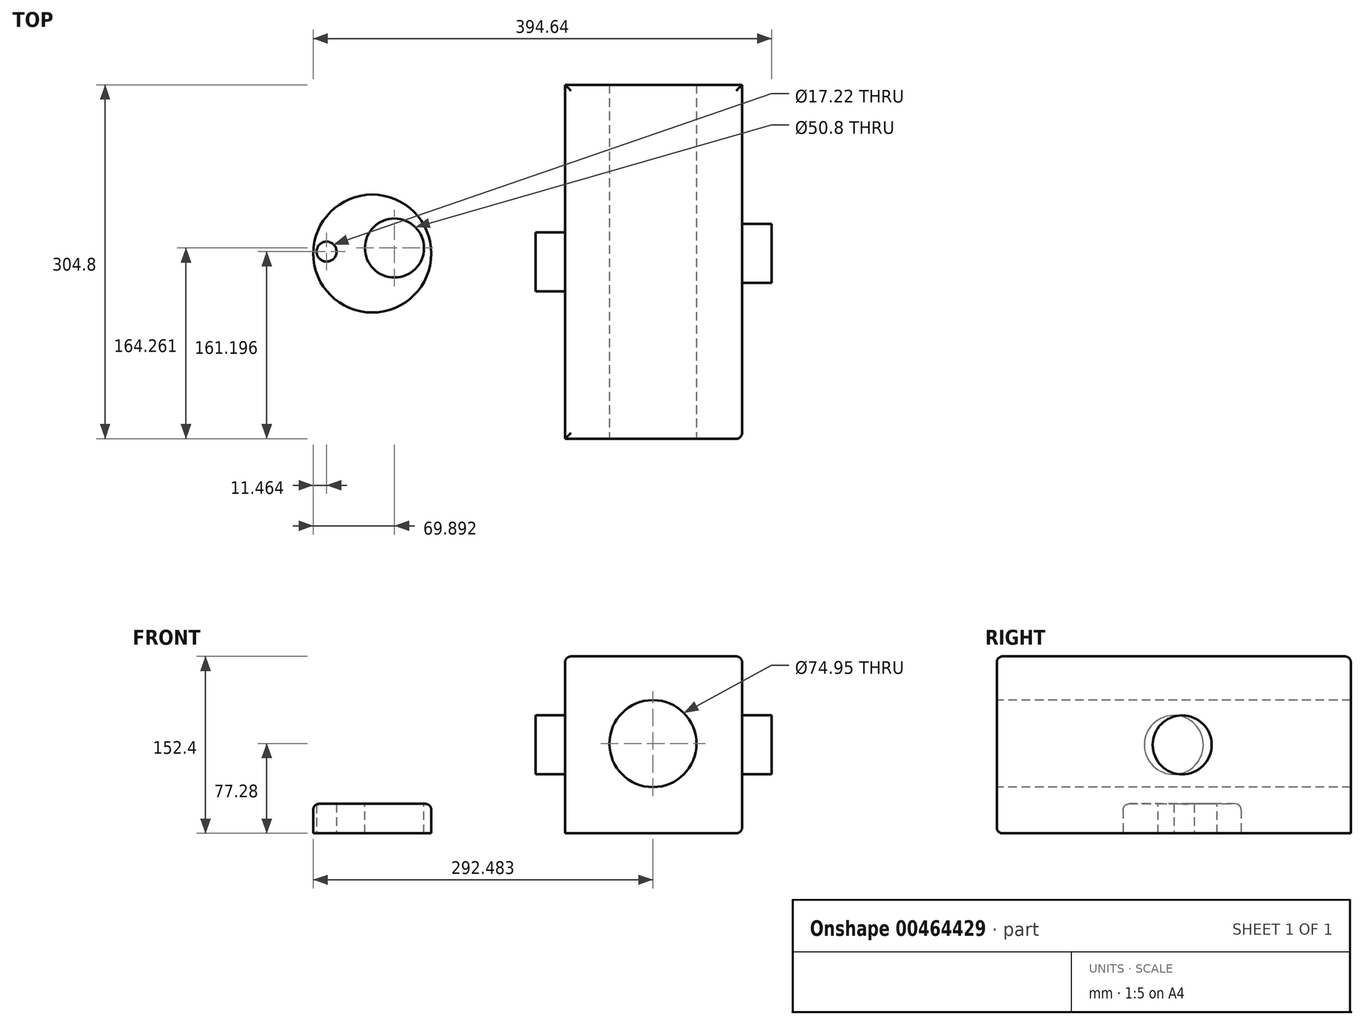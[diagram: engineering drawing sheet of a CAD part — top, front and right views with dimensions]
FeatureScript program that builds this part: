
annotation { "Feature Type Name" : "Feature", "Feature Type Description" : "" }
export const myFeature = defineFeature(function(context is Context, id is Id, definition is map)
    precondition{}
    {
        {
            var Q0;
            Q0=qCreatedBy(makeId("Top.planeOp"),FACE);
            var sketch = newSketch(context, id + "F0", { "sketchPlane" : qUnion([Q0])});
            skCircle(sketch, "E0", {"center": v(0, 0) * mm, "radius": 50.8 * mm});
            skLineSegment(sketch, "E1", {"start": v(0, 0) * mm, "end": v(-50.76, 2.14) * mm, "construction": true});
            skCircle(sketch, "E2", {"center": v(-39.34, 1.66) * mm, "radius": 8.61 * mm});
            skSolve(sketch);
        }
        {
            var Q0;
            Q0=makeQuery(id+"F0.imprint","IMPRINT",FACE,{"disambiguationData":[TD([[makeQuery(id+"F0.imprint","IMPRINT",EDGE,{"derivedFrom":sQuery(id+"F0.wireOp",EDGE,"E0")}),1.0]])]});
            extrude(context, id + "F1", {"entities" : qUnion([Q0]), "depth" : 25.4 * mm});
        }
        {
            var Q0;
            Q0=qCreatedBy(makeId("Top.planeOp"),FACE);
            var sketch = newSketch(context, id + "F2", { "sketchPlane" : qUnion([Q0])});
            skLineSegment(sketch, "E3.bottom", {"start": v(166.04, 145.26) * mm, "end": v(318.44, 145.26) * mm});
            skLineSegment(sketch, "E3.top", {"start": v(166.04, -159.54) * mm, "end": v(318.44, -159.54) * mm});
            skLineSegment(sketch, "E3.left", {"start": v(166.04, 145.26) * mm, "end": v(166.04, -159.54) * mm});
            skLineSegment(sketch, "E3.right", {"start": v(318.44, 145.26) * mm, "end": v(318.44, -159.54) * mm});
            skSolve(sketch);
        }
        {
            var Q0;
            Q0=makeQuery(id+"F2.imprint","IMPRINT",FACE,{"disambiguationData":[TD([[makeQuery(id+"F2.imprint","IMPRINT",EDGE,{"derivedFrom":sQuery(id+"F2.wireOp",EDGE,"E3.bottom")}),-1.0]])]});
            extrude(context, id + "F3", {"entities" : qUnion([Q0]), "depth" : 152.4 * mm});
        }
        {
            var Q0;
            Q0=makeQuery(id+"F3.opExtrude","SWEPT_FACE",FACE,{"disambiguationData":[OSD([sQuery(id+"F2.wireOp",EDGE,"E3.top")])]});
            var sketch = newSketch(context, id + "F4", { "sketchPlane" : qUnion([Q0])});
            skPoint(sketch, "E4.0", {"position": v(242.24, 152.4) * mm});
            skPoint(sketch, "E4.1", {"position": v(166.04, 76.2) * mm});
            skPoint(sketch, "E4.2", {"position": v(318.44, 76.2) * mm});
            skPoint(sketch, "E4.3", {"position": v(242.24, 0) * mm});
            skLineSegment(sketch, "E5", {"start": v(242.24, 152.4) * mm, "end": v(242.24, 0) * mm, "construction": true});
            skLineSegment(sketch, "E6", {"start": v(318.44, 76.2) * mm, "end": v(166.04, 76.2) * mm, "construction": true});
            skCircle(sketch, "E7", {"center": v(242.24, 76.2) * mm, "radius": 76.2 * mm});
            skSolve(sketch);
        }
        {
            var Q0;
            {var subQ0=sQuery(id+"F4.wireOp",EDGE,"E7");var subQ1=sQuery(id+"F2.wireOp",EDGE,"E3.top");var subQ2=makeQuery(id+"F4.imprint","INTERSECT",VERTEX,{"derivedFrom":[makeQuery(id+"F3.opExtrude","CAP_EDGE",EDGE,{"disambiguationData":[OSD([subQ1])],"isStart":false}),subQ0]});Q0=makeQuery(id+"F4.imprint","IMPRINT",FACE,{"disambiguationData":[TD([[makeQuery(id+"F4.imprint","IMPRINT",EDGE,{"disambiguationData":[TD([[subQ2,1.0]])],"derivedFrom":subQ0}),1.0]])]});}
            extrude(context, id + "F5", {"entities" : qUnion([Q0]), "operationType" : NewBodyOperationType.ADD, "oppositeDirection" : true, "depth" : 304.8 * mm});
        }
        {
            var Q0;
            {var subQ0=sQuery(id+"F2.wireOp",EDGE,"E3.bottom");var subQ1=sQuery(id+"F2.wireOp",EDGE,"E3.right");var subQ2=sQuery(id+"F2.wireOp",EDGE,"E3.top");Q0=makeQuery(id+"F5.boolean.opBoolean","SPLIT",FACE,{"disambiguationData":[TD([makeQuery(id+"F3.opExtrude","CAP_FACE",FACE,{"disambiguationData":[OSD([subQ0,subQ2,sQuery(id+"F2.wireOp",EDGE,"E3.left"),subQ1])],"isStart":false})])],"derivedFrom":makeQuery(id+"F3.opExtrude","SWEPT_FACE",FACE,{"disambiguationData":[OSD([subQ1])]})});}
            var sketch = newSketch(context, id + "F6", { "sketchPlane" : qUnion([Q0])});
            skCircle(sketch, "E8", {"center": v(0, 76.2) * mm, "radius": 25.4 * mm});
            skSolve(sketch);
        }
        {
            var Q0;
            {var subQ0=sQuery(id+"F6.wireOp",EDGE,"E8");var subQ1=makeQuery(id+"F5.boolean.opBoolean","INTERSECT",EDGE,{"disambiguationData":[OD(1.0)],"derivedFrom":[makeQuery(id+"F3.opExtrude","SWEPT_FACE",FACE,{"disambiguationData":[OSD([sQuery(id+"F2.wireOp",EDGE,"E3.right")])]}),makeQuery(id+"F5.opExtrude","SWEPT_FACE",FACE,{"disambiguationData":[OSD([sQuery(id+"F4.wireOp",EDGE,"E7")])]})]});var subQ2=makeQuery(id+"F6.imprint","INTERSECT",VERTEX,{"disambiguationData":[OD(0.0)],"derivedFrom":[subQ1,subQ0]});Q0=makeQuery(id+"F6.imprint","IMPRINT",FACE,{"disambiguationData":[TD([[makeQuery(id+"F6.imprint","IMPRINT",EDGE,{"disambiguationData":[TD([[subQ2,1.0]])],"derivedFrom":subQ0}),1.0]])]});}
            var Q1;
            {var subQ0=sQuery(id+"F6.wireOp",EDGE,"E8");var subQ1=makeQuery(id+"F5.boolean.opBoolean","INTERSECT",EDGE,{"disambiguationData":[OD(1.0)],"derivedFrom":[makeQuery(id+"F3.opExtrude","SWEPT_FACE",FACE,{"disambiguationData":[OSD([sQuery(id+"F2.wireOp",EDGE,"E3.right")])]}),makeQuery(id+"F5.opExtrude","SWEPT_FACE",FACE,{"disambiguationData":[OSD([sQuery(id+"F4.wireOp",EDGE,"E7")])]})]});var subQ2=makeQuery(id+"F6.imprint","INTERSECT",VERTEX,{"disambiguationData":[OD(0.0)],"derivedFrom":[subQ1,subQ0]});Q1=makeQuery(id+"F6.imprint","IMPRINT",FACE,{"disambiguationData":[TD([[makeQuery(id+"F6.imprint","IMPRINT",EDGE,{"disambiguationData":[TD([[subQ2,-1.0]])],"derivedFrom":subQ0}),1.0]])]});}
            extrude(context, id + "F7", {"entities" : qUnion([Q0, Q1]), "depth" : 25.4 * mm});
        }
        {
            var Q0;
            {var subQ0=sQuery(id+"F2.wireOp",EDGE,"E3.bottom");var subQ1=sQuery(id+"F2.wireOp",EDGE,"E3.left");var subQ2=sQuery(id+"F2.wireOp",EDGE,"E3.top");Q0=makeQuery(id+"F5.boolean.opBoolean","SPLIT",FACE,{"disambiguationData":[TD([makeQuery(id+"F3.opExtrude","CAP_FACE",FACE,{"disambiguationData":[OSD([subQ0,subQ2,subQ1,sQuery(id+"F2.wireOp",EDGE,"E3.right")])],"isStart":false})])],"derivedFrom":makeQuery(id+"F3.opExtrude","SWEPT_FACE",FACE,{"disambiguationData":[OSD([subQ1])]})});}
            var sketch = newSketch(context, id + "F8", { "sketchPlane" : qUnion([Q0])});
            skPoint(sketch, "E9.0", {"position": v(7.14, 76.2) * mm});
            skCircle(sketch, "E10", {"center": v(7.14, 76.2) * mm, "radius": 25.4 * mm});
            skSolve(sketch);
        }
        {
            var Q0;
            {var subQ0=sQuery(id+"F8.wireOp",EDGE,"E10");var subQ1=makeQuery(id+"F5.boolean.opBoolean","INTERSECT",EDGE,{"disambiguationData":[OD(1.0)],"derivedFrom":[makeQuery(id+"F3.opExtrude","SWEPT_FACE",FACE,{"disambiguationData":[OSD([sQuery(id+"F2.wireOp",EDGE,"E3.left")])]}),makeQuery(id+"F5.opExtrude","SWEPT_FACE",FACE,{"disambiguationData":[OSD([sQuery(id+"F4.wireOp",EDGE,"E7")])]})]});var subQ2=makeQuery(id+"F8.imprint","INTERSECT",VERTEX,{"disambiguationData":[OD(0.0)],"derivedFrom":[subQ1,subQ0]});Q0=makeQuery(id+"F8.imprint","IMPRINT",FACE,{"disambiguationData":[TD([[makeQuery(id+"F8.imprint","IMPRINT",EDGE,{"disambiguationData":[TD([[subQ2,-1.0]])],"derivedFrom":subQ0}),1.0]])]});}
            var Q1;
            {var subQ0=sQuery(id+"F8.wireOp",EDGE,"E10");var subQ1=makeQuery(id+"F5.boolean.opBoolean","INTERSECT",EDGE,{"disambiguationData":[OD(1.0)],"derivedFrom":[makeQuery(id+"F3.opExtrude","SWEPT_FACE",FACE,{"disambiguationData":[OSD([sQuery(id+"F2.wireOp",EDGE,"E3.left")])]}),makeQuery(id+"F5.opExtrude","SWEPT_FACE",FACE,{"disambiguationData":[OSD([sQuery(id+"F4.wireOp",EDGE,"E7")])]})]});var subQ2=makeQuery(id+"F8.imprint","INTERSECT",VERTEX,{"disambiguationData":[OD(0.0)],"derivedFrom":[subQ1,subQ0]});Q1=makeQuery(id+"F8.imprint","IMPRINT",FACE,{"disambiguationData":[TD([[makeQuery(id+"F8.imprint","IMPRINT",EDGE,{"disambiguationData":[TD([[subQ2,1.0]])],"derivedFrom":subQ0}),1.0]])]});}
            extrude(context, id + "F9", {"entities" : qUnion([Q0, Q1]), "depth" : 25.4 * mm});
        }
        {
            var Q0;
            {var subQ0=sQuery(id+"F4.wireOp",EDGE,"E7");var subQ1=sQuery(id+"F2.wireOp",EDGE,"E3.top");var subQ2=makeQuery(id+"F4.imprint","INTERSECT",VERTEX,{"derivedFrom":[makeQuery(id+"F3.opExtrude","CAP_EDGE",EDGE,{"disambiguationData":[OSD([subQ1])],"isStart":false}),subQ0]});Q0=makeQuery(id+"F4.imprint","IMPRINT",FACE,{"disambiguationData":[TD([[makeQuery(id+"F4.imprint","IMPRINT",EDGE,{"disambiguationData":[TD([[subQ2,1.0]])],"derivedFrom":subQ0}),1.0]])]});}
            var sketch = newSketch(context, id + "F10", { "sketchPlane" : qUnion([Q0])});
            skCircle(sketch, "E11", {"center": v(241.68, 77.28) * mm, "radius": 37.48 * mm});
            skSolve(sketch);
        }
        {
            var Q0;
            Q0=makeQuery(id+"F10.imprint","IMPRINT",FACE,{"disambiguationData":[TD([[makeQuery(id+"F10.imprint","IMPRINT",EDGE,{"derivedFrom":sQuery(id+"F10.wireOp",EDGE,"E11")}),1.0]])]});
            var Q1;
            Q1=sQuery(id+"F10.wireOp",EDGE,"E11");
            extrude(context, id + "F11", {"entities" : qUnion([Q0]), "operationType" : NewBodyOperationType.REMOVE, "surfaceEntities" : qUnion([Q1]), "oppositeDirection" : true, "depth" : 1270 * mm});
        }
        {
            var Q0;
            Q0 = qSketchRegion(id + "F8", true);
            var Q1;
            Q1 = qSketchRegion(id + "F6", true);
            extrude(context, id + "F12", {"entities" : qUnion([Q0, Q1]), "operationType" : NewBodyOperationType.ADD, "oppositeDirection" : true, "depth" : 25.4 * mm});
        }
        {
            var Q0;
            Q0=makeQuery(id+"F8.imprint","IMPRINT",FACE,{"disambiguationData":[TD([[makeQuery(id+"F8.imprint","IMPRINT",EDGE,{"derivedFrom":sQuery(id+"F8.wireOp",EDGE,"E10")}),1.0]])]});
            extrude(context, id + "F13", {"entities" : qUnion([Q0]), "operationType" : NewBodyOperationType.ADD, "depth" : 25.4 * mm});
        }
        {
            var Q0;
            Q0=makeQuery(id+"F1.opExtrude","CAP_FACE",FACE,{"disambiguationData":[OSD([sQuery(id+"F0.wireOp",EDGE,"E0"),sQuery(id+"F0.wireOp",EDGE,"E2")])],"isStart":false});
            var sketch = newSketch(context, id + "F14", { "sketchPlane" : qUnion([Q0])});
            skCircle(sketch, "E12", {"center": v(19.1, 4.72) * mm, "radius": 25.4 * mm});
            skSolve(sketch);
        }
        {
            var Q0;
            Q0=makeQuery(id+"F14.imprint","IMPRINT",FACE,{"disambiguationData":[TD([[makeQuery(id+"F14.imprint","IMPRINT",EDGE,{"derivedFrom":sQuery(id+"F14.wireOp",EDGE,"E12")}),1.0]])]});
            extrude(context, id + "F15", {"entities" : qUnion([Q0]), "operationType" : NewBodyOperationType.REMOVE, "oppositeDirection" : true, "depth" : 25.4 * mm});
        }
        {
            var Q0;
            Q0=makeQuery(id+"F15.boolean.opBoolean","COPY",EDGE,{"derivedFrom":makeQuery(id+"F15.opExtrude","CAP_EDGE",EDGE,{"disambiguationData":[OSD([sQuery(id+"F14.wireOp",EDGE,"E12")])],"isStart":true})});
            var Q1;
            Q1=makeQuery(id+"F12.opExtrude","CAP_EDGE",EDGE,{"disambiguationData":[OSD([sQuery(id+"F6.wireOp",EDGE,"E8")])],"isStart":false});
            var Q2;
            Q2=makeQuery(id+"F3.opExtrude","CAP_EDGE",EDGE,{"disambiguationData":[OSD([sQuery(id+"F2.wireOp",EDGE,"E3.top")])],"isStart":false});
            var Q3;
            Q3=makeQuery(id+"F3.opExtrude","CAP_FACE",FACE,{"disambiguationData":[OSD([sQuery(id+"F2.wireOp",EDGE,"E3.bottom"),sQuery(id+"F2.wireOp",EDGE,"E3.top"),sQuery(id+"F2.wireOp",EDGE,"E3.left"),sQuery(id+"F2.wireOp",EDGE,"E3.right")])],"isStart":false});
            var Q4;
            Q4=makeQuery(id+"F3.opExtrude","SWEPT_EDGE",EDGE,{"disambiguationData":[OSD([sQuery(id+"F2.wireOp",EDGE,"E3.top"),sQuery(id+"F2.wireOp",EDGE,"E3.right")])]});
            var Q5;
            Q5=makeQuery(id+"F3.opExtrude","CAP_EDGE",EDGE,{"disambiguationData":[OSD([sQuery(id+"F2.wireOp",EDGE,"E3.right")])],"isStart":true});
            var Q6;
            Q6=makeQuery(id+"F3.opExtrude","CAP_EDGE",EDGE,{"disambiguationData":[OSD([sQuery(id+"F2.wireOp",EDGE,"E3.top")])],"isStart":true});
            var Q7;
            Q7=makeQuery(id+"F11.boolean.opBoolean","COPY",EDGE,{"derivedFrom":makeQuery(id+"F11.opExtrude","CAP_EDGE",EDGE,{"disambiguationData":[OSD([sQuery(id+"F10.wireOp",EDGE,"E11")])],"isStart":true})});
            var Q8;
            Q8=makeQuery(id+"F1.opExtrude","CAP_EDGE",EDGE,{"disambiguationData":[OSD([sQuery(id+"F0.wireOp",EDGE,"E0")])],"isStart":false});
            fillet(context, id + "F16", {"entities" : qUnion([Q0, Q1, Q2, Q3, Q4, Q5, Q6, Q7, Q8]), "radius" : 5.08 * mm, "tangentPropagation" : true, "allowEdgeOverflow" : false});
        }
    });
